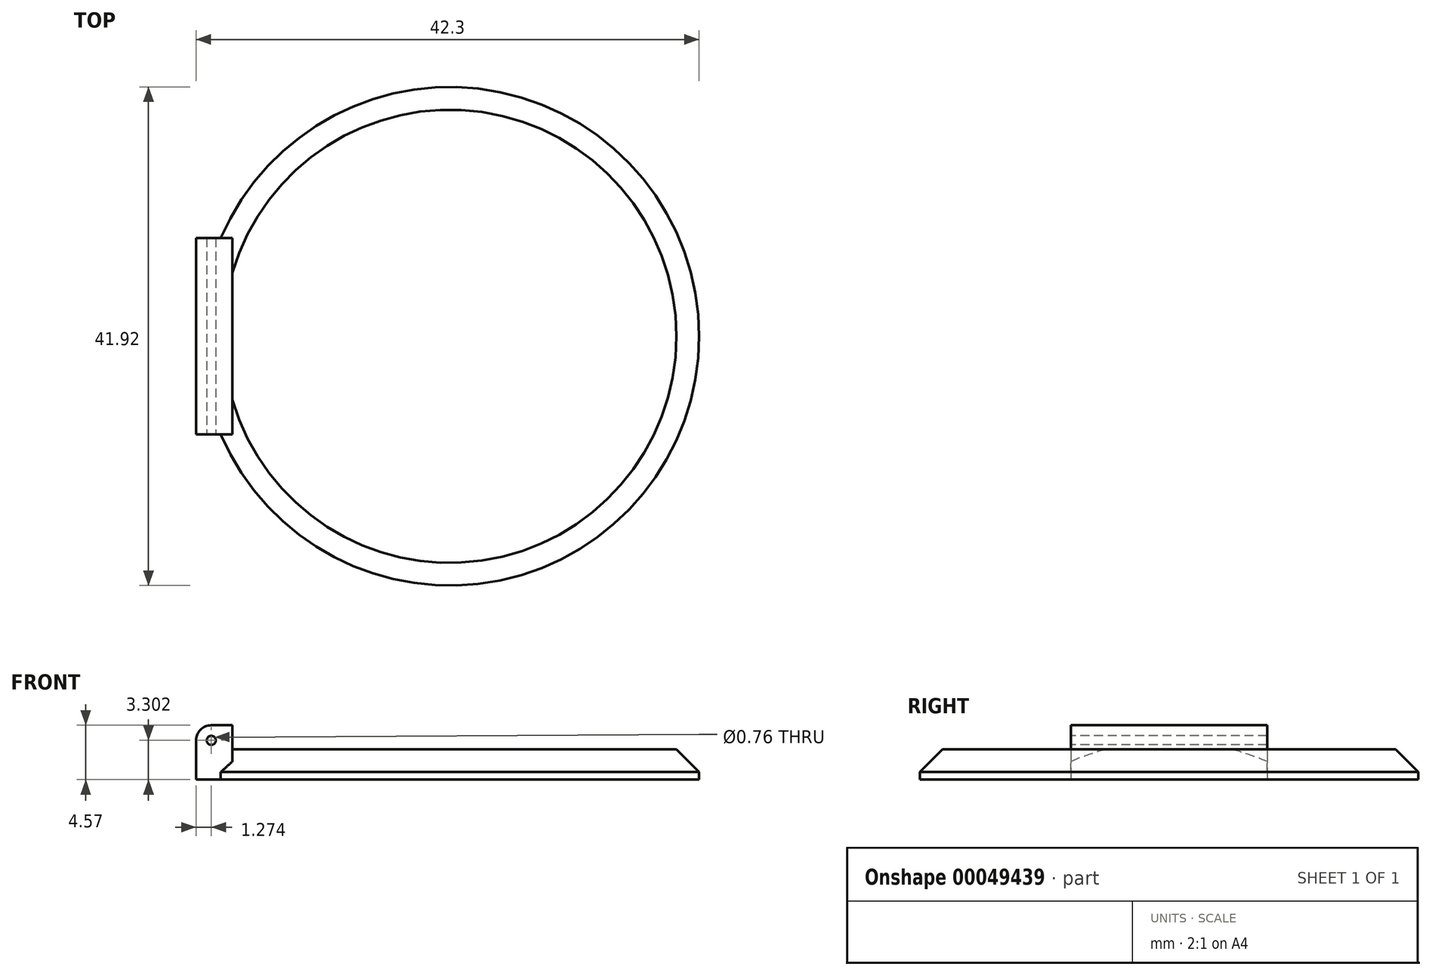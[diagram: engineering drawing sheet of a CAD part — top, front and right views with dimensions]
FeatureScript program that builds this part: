
annotation { "Feature Type Name" : "Feature", "Feature Type Description" : "" }
export const myFeature = defineFeature(function(context is Context, id is Id, definition is map)
    precondition{}
    {
        {
            var Q0;
            Q0=qCreatedBy(makeId("Top.planeOp"),FACE);
            var sketch = newSketch(context, id + "F0", { "sketchPlane" : qUnion([Q0])});
            skCircle(sketch, "E0", {"center": v(0, 0) * mm, "radius": 20.96 * mm});
            skSolve(sketch);
        }
        {
            var Q0;
            Q0=makeQuery(id+"F0.imprint","IMPRINT",FACE,{"disambiguationData":[TD([[makeQuery(id+"F0.imprint","IMPRINT",EDGE,{"derivedFrom":sQuery(id+"F0.wireOp",EDGE,"E0")}),1.0]])]});
            extrude(context, id + "F1", {"entities" : qUnion([Q0]), "depth" : 2.54 * mm});
        }
        {
            var Q0;
            Q0=makeQuery(id+"F1.opExtrude","CAP_EDGE",EDGE,{"disambiguationData":[OSD([sQuery(id+"F0.wireOp",EDGE,"E0")])],"isStart":false});
            chamfer(context, id + "F2", {"entities" : qUnion([Q0]), "width" : 1.9 * mm, "tangentPropagation" : true});
        }
        {
            var Q0;
            Q0=qCreatedBy(makeId("Top.planeOp"),FACE);
            var sketch = newSketch(context, id + "F3", { "sketchPlane" : qUnion([Q0])});
            skLineSegment(sketch, "E1.rect.bottom", {"start": v(-18.29, -8.26) * mm, "end": v(-21.34, -8.26) * mm});
            skLineSegment(sketch, "E1.rect.top", {"start": v(-18.29, 8.26) * mm, "end": v(-21.34, 8.26) * mm});
            skLineSegment(sketch, "E1.rect.left", {"start": v(-18.29, -8.26) * mm, "end": v(-18.29, 8.26) * mm});
            skLineSegment(sketch, "E1.rect.right", {"start": v(-21.34, -8.26) * mm, "end": v(-21.34, 8.26) * mm});
            skPoint(sketch, "E1.rect.middle", {"position": v(-19.81, 0) * mm});
            skLineSegment(sketch, "E2", {"start": v(0, 0) * mm, "end": v(-19.81, 0) * mm, "construction": true});
            skSolve(sketch);
        }
        {
            var Q0;
            Q0=makeQuery(id+"F3.imprint","IMPRINT",FACE,{"disambiguationData":[TD([[makeQuery(id+"F3.imprint","IMPRINT",EDGE,{"derivedFrom":sQuery(id+"F3.wireOp",EDGE,"E1.rect.bottom")}),-1.0]])]});
            extrude(context, id + "F4", {"entities" : qUnion([Q0]), "operationType" : NewBodyOperationType.ADD, "depth" : 4.57 * mm});
        }
        {
            var Q0;
            Q0=makeQuery(id+"F4.opExtrude","CAP_EDGE",EDGE,{"disambiguationData":[OSD([sQuery(id+"F3.wireOp",EDGE,"E1.rect.right")])],"isStart":false});
            fillet(context, id + "F5", {"entities" : qUnion([Q0]), "radius" : 1.27 * mm, "tangentPropagation" : true, "allowEdgeOverflow" : false});
        }
        {
            var Q0;
            Q0=makeQuery(id+"F4.opExtrude","SWEPT_FACE",FACE,{"disambiguationData":[OSD([sQuery(id+"F3.wireOp",EDGE,"E1.rect.bottom")])]});
            var sketch = newSketch(context, id + "F6", { "sketchPlane" : qUnion([Q0])});
            skLineSegment(sketch, "E3", {"start": v(-20.07, 4.57) * mm, "end": v(-20.07, 3.3) * mm, "construction": true});
            skCircle(sketch, "E4", {"center": v(-20.07, 3.3) * mm, "radius": 0.38 * mm});
            skSolve(sketch);
        }
        {
            var Q0;
            Q0=makeQuery(id+"F6.imprint","IMPRINT",FACE,{"disambiguationData":[TD([[makeQuery(id+"F6.imprint","IMPRINT",EDGE,{"derivedFrom":sQuery(id+"F6.wireOp",EDGE,"E4")}),1.0]])]});
            extrude(context, id + "F7", {"entities" : qUnion([Q0]), "operationType" : NewBodyOperationType.REMOVE, "oppositeDirection" : true, "depth" : 25.4 * mm});
        }
    });
